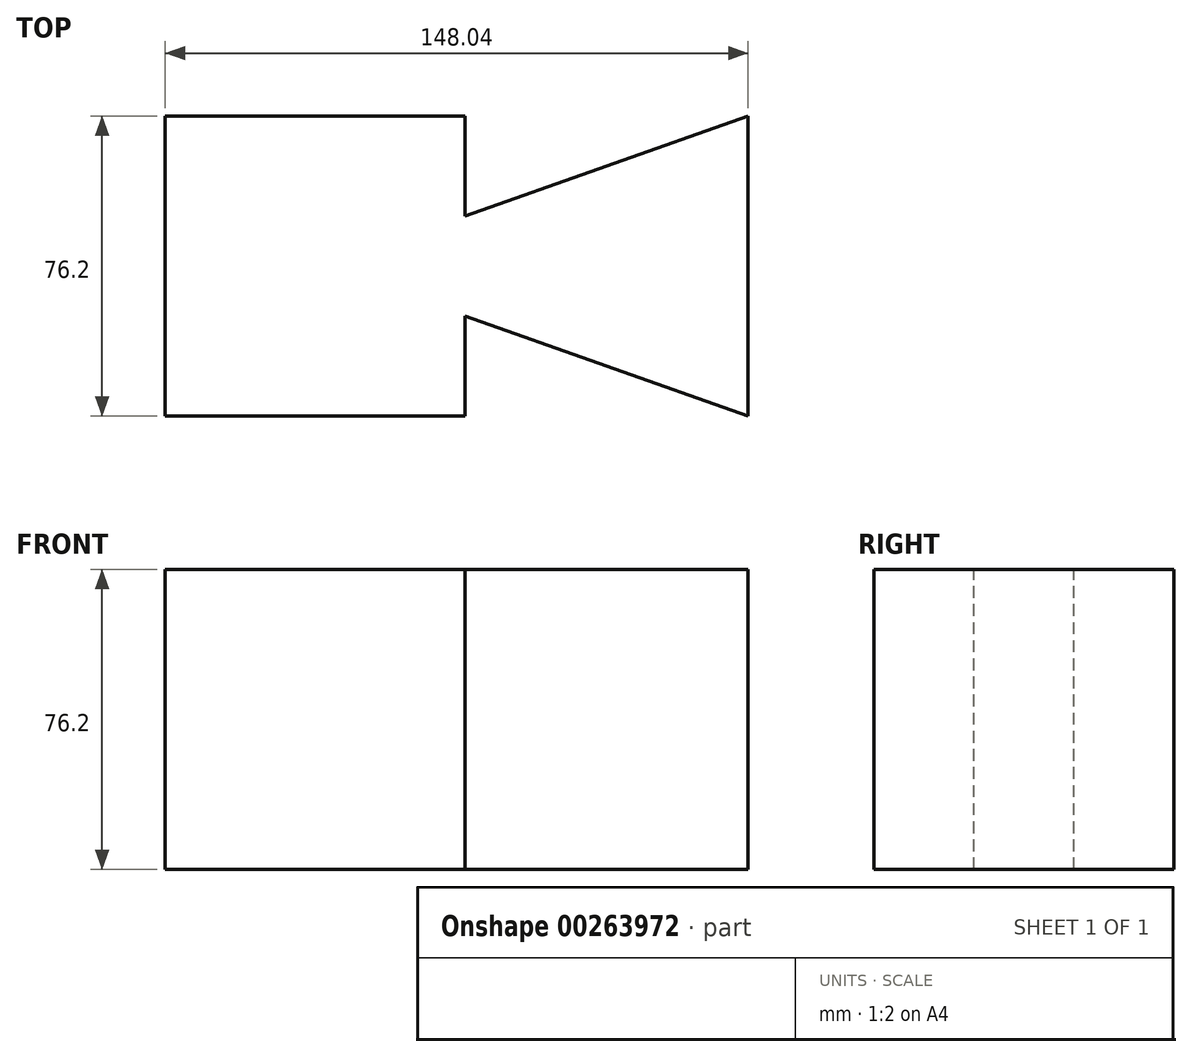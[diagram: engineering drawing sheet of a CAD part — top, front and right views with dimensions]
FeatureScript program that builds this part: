
annotation { "Feature Type Name" : "Feature", "Feature Type Description" : "" }
export const myFeature = defineFeature(function(context is Context, id is Id, definition is map)
    precondition{}
    {
        {
            var Q0;
            Q0=qCreatedBy(makeId("Top.planeOp"),FACE);
            var sketch = newSketch(context, id + "F0", { "sketchPlane" : qUnion([Q0])});
            skLineSegment(sketch, "E0", {"start": v(-76.2, 0) * mm, "end": v(-76.2, 76.2) * mm});
            skLineSegment(sketch, "E1", {"start": v(-76.2, 76.2) * mm, "end": v(0, 76.2) * mm});
            skLineSegment(sketch, "E2", {"start": v(0, 76.2) * mm, "end": v(0, 0) * mm});
            skLineSegment(sketch, "E3", {"start": v(0, 0) * mm, "end": v(-76.2, 0) * mm});
            skLineSegment(sketch, "E4", {"start": v(0, 76.2) * mm, "end": v(0, 50.8) * mm});
            skLineSegment(sketch, "E5", {"start": v(0, 0) * mm, "end": v(0, 25.4) * mm});
            skLineSegment(sketch, "E6", {"start": v(0, 25.4) * mm, "end": v(71.84, 0) * mm});
            skLineSegment(sketch, "E7", {"start": v(0, 50.8) * mm, "end": v(71.84, 76.2) * mm});
            skLineSegment(sketch, "E8", {"start": v(71.84, 76.2) * mm, "end": v(71.84, 0) * mm});
            skSolve(sketch);
        }
        {
            var Q0;
            Q0=makeQuery(id+"F0.imprint","IMPRINT",FACE,{"disambiguationData":[TD([[makeQuery(id+"F0.imprint","IMPRINT",EDGE,{"derivedFrom":sQuery(id+"F0.wireOp",EDGE,"E2")}),1.0]])]});
            var Q1;
            Q1 = qSketchRegion(id + "F0", true);
            extrude(context, id + "F1", {"entities" : qUnion([Q0, Q1]), "oppositeDirection" : true, "depth" : 76.2 * mm});
        }
    });
